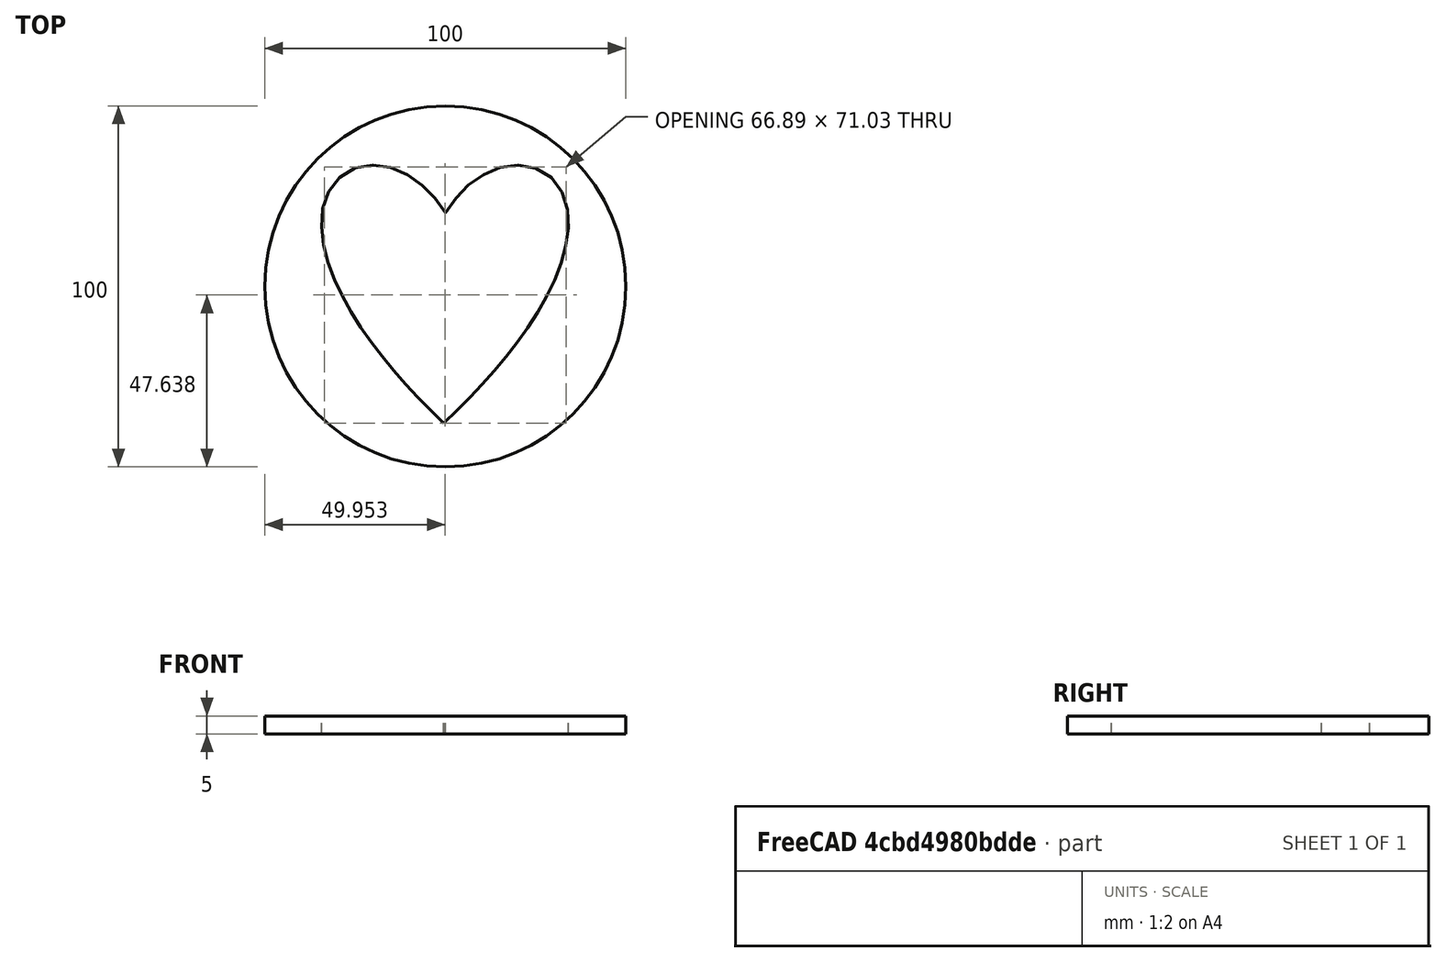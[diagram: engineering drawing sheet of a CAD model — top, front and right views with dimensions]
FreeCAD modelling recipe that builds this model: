
FCSTD DOCUMENT  (FreeCAD 0.20R29177 +426 (Git))
Label: moneda_corazon
License: Creative Commons Attribution-ShareAlike
LicenseURL: http://creativecommons.org/licenses/by-sa/4.0/
objects: Sketcher::SketchObject×1, Part::Cylinder×1, Part::Extrusion×1, Part::Cut×1
note: 4 computed .brp shape members not serialized (recipe doc carries the construction recipe); baked Part::Feature solids carry a one-line shape summary decoded from their .brp

FEATURE [Sketcher::SketchObject] Sketch
  FullyConstrained = false
  sketch-geometry (14):
    g0-g3: Circle x4 (B-spline internal-alignment scaffolding for g4; pole/knot coordinates omitted)
    g4: BSplineCurve PolesCount=4 KnotsCount=2 Degree=3 IsPeriodic=0
    g5: GeomPoint X=0 Y=20.3714 Z=0
    g6: GeomPoint X=-0.43936 Y=-37.8768 Z=0
    g7-g10: Circle x4 (B-spline internal-alignment scaffolding for g11; pole/knot coordinates omitted)
    g11: BSplineCurve PolesCount=4 KnotsCount=2 Degree=3 IsPeriodic=0
    g12: GeomPoint X=0 Y=20.3714 Z=0
    g13: GeomPoint X=-0.43936 Y=-37.8768 Z=0
  constraints (19):
    c: PointOnObject(g4,g-2)
    c: Weight(g0) = 1
    c: Equal(g0,g1)
    c: Equal(g0,g2)
    c: Equal(g0,g3)
    c: InternalAlignment(g0-g3 -> g4) x4
    c: InternalAlignment(g5,g4)
    c: InternalAlignment(g6,g4)
    c: Weight(g7) = 1
    c: Coincident(g11,g4)
    c: Equal(g7,g8)
    c: Equal(g7,g9)
    c: Equal(g7,g10)
    c: Coincident(g11,g4)
    c: InternalAlignment(g7-g10 -> g11) x4
    c: InternalAlignment(g12,g11)
    c: InternalAlignment(g13,g11)
    c: Symmetric(g9,g2,g-2)
    c: Symmetric(g8,g1,g-2)
FEATURE [Part::Cylinder] Cylinder  label="Cilindro"
  Angle = 360
  AttacherType = Attacher::AttachEngine3D
  FirstAngle = 0
  Height = 5
  Radius = 50
  SecondAngle = 0
FEATURE [Part::Extrusion] Extrude
  Base = -> Sketch
  Dir = (0,0,1)
  DirMode = 2
  FaceMakerClass = Part::FaceMakerBullseye
  LengthFwd = 6
  LengthRev = 1
  Solid = true
  Symmetric = false
FEATURE [Part::Cut] Cut
  Base = -> Cylinder
  Tool = -> Extrude
